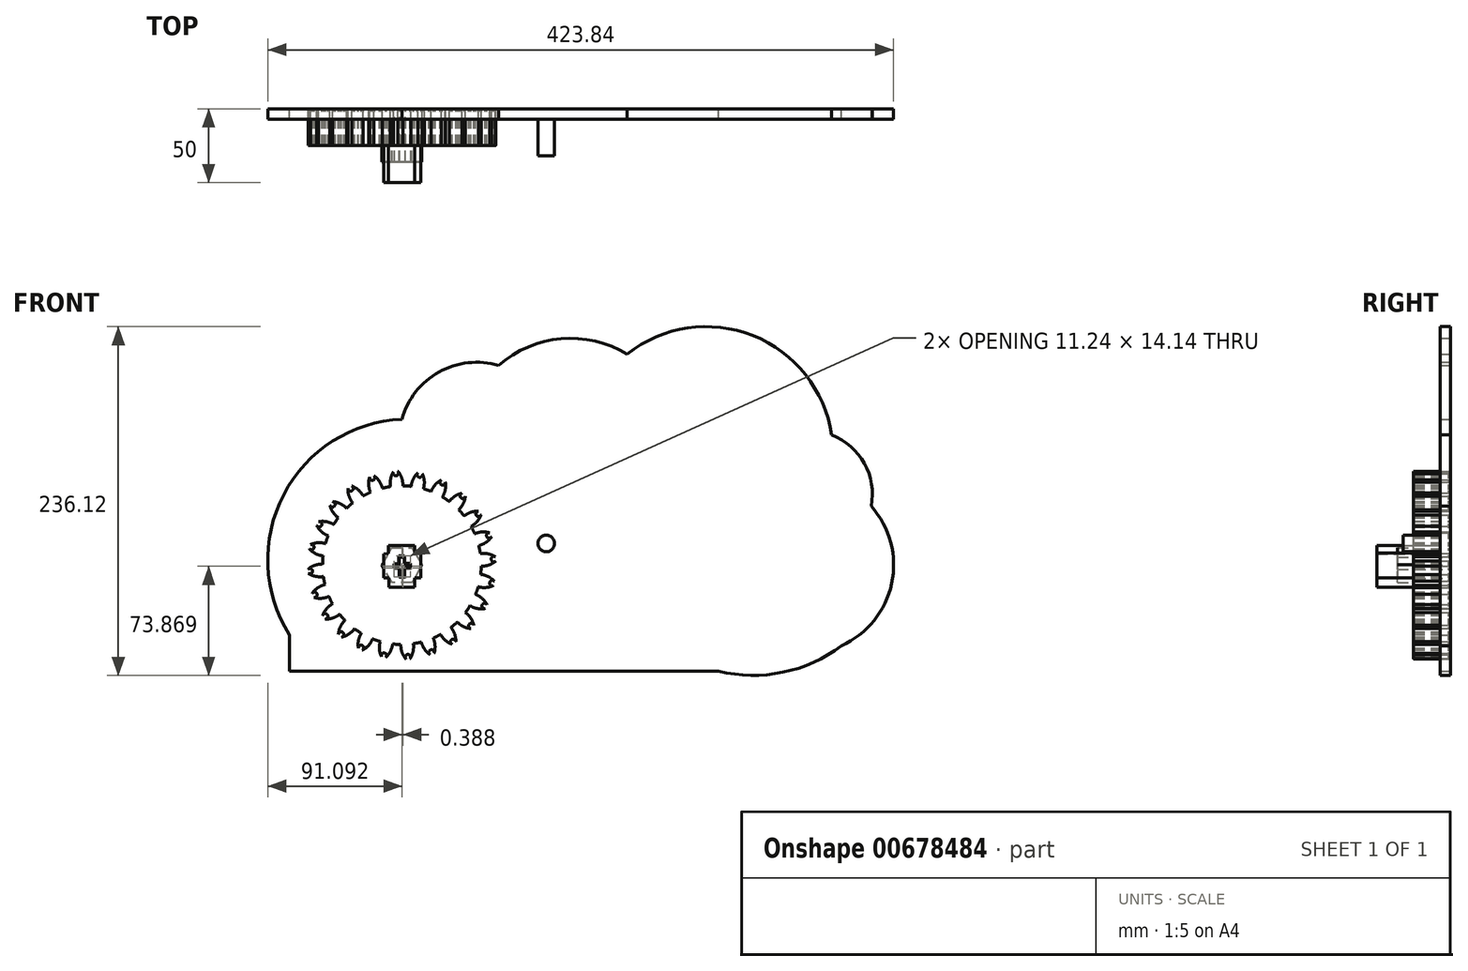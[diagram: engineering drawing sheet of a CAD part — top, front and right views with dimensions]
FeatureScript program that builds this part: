
annotation { "Feature Type Name" : "Feature", "Feature Type Description" : "" }
export const myFeature = defineFeature(function(context is Context, id is Id, definition is map)
    precondition{}
    {
        {
            var Q0;
            Q0=qCreatedBy(makeId("Front.planeOp"),FACE);
            var sketch = newSketch(context, id + "F0", { "sketchPlane" : qUnion([Q0])});
            skCircle(sketch, "E0", {"center": v(0, 0) * mm, "radius": 58.67 * mm, "construction": true});
            skCircle(sketch, "E1", {"center": v(0, 0) * mm, "radius": 53.72 * mm});
            skCircle(sketch, "E2", {"center": v(0, 0) * mm, "radius": 63.5 * mm, "construction": true});
            skLineSegment(sketch, "E3", {"start": v(0, 0) * mm, "end": v(0, 86.23) * mm, "construction": true});
            skLineSegment(sketch, "E4", {"start": v(0, 0) * mm, "end": v(-6, 91.64) * mm, "construction": true});
            skLineSegment(sketch, "E5", {"start": v(0, 58.67) * mm, "end": v(-65.6, 60.5) * mm, "construction": true});
            skLineSegment(sketch, "E6", {"start": v(0, 58.67) * mm, "end": v(-64.31, 37.28) * mm, "construction": true});
            skCircle(sketch, "E7", {"center": v(0, 0) * mm, "radius": 55.67 * mm, "construction": true});
            skCircle(sketch, "E8", {"center": v(0, 58.67) * mm, "radius": 14.6 * mm, "construction": true});
            skCircle(sketch, "E9", {"center": v(-13.86, 54.06) * mm, "radius": 14.6 * mm, "construction": true});
            skArc(sketch, "E10", {"start": v(0, 58.67) * mm, "mid": v(-1.1, 61.19) * mm, "end": v(-2.66, 63.44) * mm});
            skArc(sketch, "E11", {"start": v(0.74, 53.72) * mm, "mid": v(0.58, 56.23) * mm, "end": v(0, 58.67) * mm});
            skArc(sketch, "E12.MirrorCS", {"start": v(-7.66, 58.17) * mm, "mid": v(-6.9, 60.8) * mm, "end": v(-5.64, 63.25) * mm});
            skArc(sketch, "E13.MirrorCS", {"start": v(-7.75, 53.16) * mm, "mid": v(-7.91, 55.67) * mm, "end": v(-7.66, 58.17) * mm});
            skArc(sketch, "E14", {"start": v(-5.64, 63.25) * mm, "mid": v(-3.96, 60.49) * mm, "end": v(-2.66, 63.44) * mm});
            skCircle(sketch, "E15", {"center": v(0, 0) * mm, "radius": 37.66 * mm});
            skCircle(sketch, "E16.cCircle", {"center": v(0, 0) * mm, "radius": 13.56 * mm, "construction": true});
            skLineSegment(sketch, "E16.0", {"start": v(6.65, 11.81) * mm, "end": v(13.56, 0.15) * mm});
            skLineSegment(sketch, "E16.1", {"start": v(13.56, 0.15) * mm, "end": v(6.9, -11.66) * mm});
            skLineSegment(sketch, "E16.2", {"start": v(6.9, -11.66) * mm, "end": v(-6.65, -11.81) * mm});
            skLineSegment(sketch, "E16.3", {"start": v(-6.65, -11.81) * mm, "end": v(-13.56, -0.15) * mm});
            skLineSegment(sketch, "E16.4", {"start": v(-13.56, -0.15) * mm, "end": v(-6.9, 11.66) * mm});
            skLineSegment(sketch, "E16.5", {"start": v(-6.9, 11.66) * mm, "end": v(6.65, 11.81) * mm});
            skLineSegment(sketch, "E17", {"start": v(-1.68, 5.23) * mm, "end": v(2.17, 5.23) * mm});
            skLineSegment(sketch, "E18", {"start": v(2.17, 5.23) * mm, "end": v(2.17, 0) * mm});
            skLineSegment(sketch, "E19", {"start": v(-1.68, 5.23) * mm, "end": v(-1.68, 0) * mm});
            skLineSegment(sketch, "E20", {"start": v(2.17, 0) * mm, "end": v(6.24, 0) * mm});
            skLineSegment(sketch, "E21", {"start": v(6.24, 0) * mm, "end": v(6.24, -2.8) * mm});
            skLineSegment(sketch, "E22", {"start": v(6.24, -2.8) * mm, "end": v(2.17, -2.8) * mm});
            skLineSegment(sketch, "E23", {"start": v(2.17, -2.8) * mm, "end": v(2.17, -8.9) * mm});
            skLineSegment(sketch, "E24", {"start": v(2.17, -8.9) * mm, "end": v(-1.47, -8.9) * mm});
            skLineSegment(sketch, "E25", {"start": v(-1.47, -8.9) * mm, "end": v(-1.47, -2.8) * mm});
            skLineSegment(sketch, "E26", {"start": v(-1.47, -2.8) * mm, "end": v(-5, -2.8) * mm});
            skLineSegment(sketch, "E27", {"start": v(-5, -2.8) * mm, "end": v(-5, 0) * mm});
            skLineSegment(sketch, "E28", {"start": v(-5, -0.13) * mm, "end": v(-1.68, 0) * mm});
            skSolve(sketch);
        }
        {
            var Q0;
            {var subQ0=sQuery(id+"F0.wireOp",EDGE,"E1");var subQ1=makeQuery(id+"F0.imprint","INTERSECT",VERTEX,{"derivedFrom":[subQ0,sQuery(id+"F0.wireOp",EDGE,"E11")]});Q0=makeQuery(id+"F0.imprint","IMPRINT",FACE,{"disambiguationData":[TD([[makeQuery(id+"F0.imprint","IMPRINT",EDGE,{"disambiguationData":[TD([[subQ1,-1.0]])],"derivedFrom":subQ0}),1.0]])]});}
            var Q1;
            Q1=makeQuery(id+"F0.imprint","IMPRINT",FACE,{"disambiguationData":[TD([[makeQuery(id+"F0.imprint","IMPRINT",EDGE,{"derivedFrom":sQuery(id+"F0.wireOp",EDGE,"E10")}),1.0]])]});
            var Q2;
            Q2=makeQuery(id+"F0.imprint","IMPRINT",FACE,{"disambiguationData":[TD([[makeQuery(id+"F0.imprint","IMPRINT",EDGE,{"derivedFrom":sQuery(id+"F0.wireOp",EDGE,"E15")}),1.0]])]});
            extrude(context, id + "F1", {"entities" : qUnion([Q0, Q1, Q2]), "depth" : 25 * mm, "offsetDistance" : 25 * mm});
        }
        {
            var Q0;
            Q0=makeQuery(id+"F1.opExtrude","SWEPT_BODY",BODY,{"disambiguationData":[OSD([sQuery(id+"F0.wireOp",EDGE,"E1"),sQuery(id+"F0.wireOp",EDGE,"E10"),sQuery(id+"F0.wireOp",EDGE,"E11"),sQuery(id+"F0.wireOp",EDGE,"E12.MirrorCS"),sQuery(id+"F0.wireOp",EDGE,"E13.MirrorCS"),sQuery(id+"F0.wireOp",EDGE,"E14")])]});
            var Q1;
            Q1=makeQuery(id+"F1.opExtrude","SWEPT_FACE",FACE,{"disambiguationData":[OSD([sQuery(id+"F0.wireOp",EDGE,"E1")])]});
            circularPattern(context, id + "F2", {"entities" : qUnion([Q0]), "axis" : qUnion([Q1]), "angle" : 360 * degree, "instanceCount" : 24, "equalSpace" : true});
        }
        {
            var Q0;
            Q0=makeQuery(id+"F0.imprint","IMPRINT",FACE,{"disambiguationData":[TD([[makeQuery(id+"F0.imprint","IMPRINT",EDGE,{"derivedFrom":sQuery(id+"F0.wireOp",EDGE,"E16.0")}),-1.0]])]});
            extrude(context, id + "F3", {"entities" : qUnion([Q0]), "operationType" : NewBodyOperationType.ADD, "depth" : 36 * mm, "offsetDistance" : 25 * mm});
        }
        {
            var Q0;
            Q0=qCreatedBy(makeId("Front.planeOp"),FACE);
            var sketch = newSketch(context, id + "F4", { "sketchPlane" : qUnion([Q0])});
            skLineSegment(sketch, "E29", {"start": v(-76.16, -71.82) * mm, "end": v(215.95, -71.82) * mm});
            skLineSegment(sketch, "E30", {"start": v(-76.16, -71.82) * mm, "end": v(-76.16, -47.21) * mm});
            skArc(sketch, "E31", {"start": v(0, 98.8) * mm, "mid": v(-80.06, 47.7) * mm, "end": v(-76.16, -47.21) * mm});
            skArc(sketch, "E32", {"start": v(65.52, 135.17) * mm, "mid": v(25.12, 130.75) * mm, "end": v(0, 98.8) * mm});
            skArc(sketch, "E33", {"start": v(152.61, 142.93) * mm, "mid": v(107.8, 153.27) * mm, "end": v(65.52, 135.17) * mm});
            skArc(sketch, "E34", {"start": v(290.98, 88.07) * mm, "mid": v(237.63, 155.43) * mm, "end": v(152.61, 142.93) * mm});
            skArc(sketch, "E35", {"start": v(317.8, 39.91) * mm, "mid": v(313.19, 68.89) * mm, "end": v(290.98, 88.07) * mm});
            skArc(sketch, "E36", {"start": v(297.68, -54.57) * mm, "mid": v(331.67, -12.42) * mm, "end": v(317.8, 39.91) * mm});
            skArc(sketch, "E37", {"start": v(214.46, -71.82) * mm, "mid": v(258.02, -72.58) * mm, "end": v(297.68, -54.57) * mm});
            skLineSegment(sketch, "E38", {"start": v(-2.07, 6.3) * mm, "end": v(1.78, 6.3) * mm});
            skLineSegment(sketch, "E39", {"start": v(1.78, 6.3) * mm, "end": v(1.78, 1.07) * mm});
            skLineSegment(sketch, "E40", {"start": v(-2.07, 6.3) * mm, "end": v(-2.07, 1.07) * mm});
            skLineSegment(sketch, "E41", {"start": v(1.78, 1.07) * mm, "end": v(5.85, 1.07) * mm});
            skLineSegment(sketch, "E42", {"start": v(5.85, 1.07) * mm, "end": v(5.85, -1.74) * mm});
            skLineSegment(sketch, "E43", {"start": v(5.85, -1.74) * mm, "end": v(1.78, -1.74) * mm});
            skLineSegment(sketch, "E44", {"start": v(1.78, -1.74) * mm, "end": v(1.78, -7.84) * mm});
            skLineSegment(sketch, "E45", {"start": v(1.78, -7.84) * mm, "end": v(-1.86, -7.84) * mm});
            skLineSegment(sketch, "E46", {"start": v(-1.86, -7.84) * mm, "end": v(-1.86, -1.74) * mm});
            skLineSegment(sketch, "E47", {"start": v(-1.86, -1.74) * mm, "end": v(-5.4, -1.74) * mm});
            skLineSegment(sketch, "E48", {"start": v(-5.4, -1.74) * mm, "end": v(-5.4, 1.07) * mm});
            skLineSegment(sketch, "E49", {"start": v(-5.4, 0.94) * mm, "end": v(-2.07, 1.07) * mm});
            skSolve(sketch);
        }
        {
            var Q0;
            {var subQ0=sQuery(id+"F4.wireOp",EDGE,"E30");Q0=makeQuery(id+"F4.imprint","IMPRINT",FACE,{"disambiguationData":[TD([[makeQuery(id+"F4.imprint","IMPRINT",EDGE,{"derivedFrom":subQ0}),-1.0]])]});}
            extrude(context, id + "F5", {"entities" : qUnion([Q0]), "depth" : 50 * mm, "offsetDistance" : 25 * mm});
        }
        {
            var Q0;
            Q0=makeQuery(id+"F5.opExtrude","CAP_FACE",FACE,{"disambiguationData":[OSD([sQuery(id+"F4.wireOp",EDGE,"E29"),sQuery(id+"F4.wireOp",EDGE,"E30"),sQuery(id+"F4.wireOp",EDGE,"E31"),sQuery(id+"F4.wireOp",EDGE,"E32"),sQuery(id+"F4.wireOp",EDGE,"E33"),sQuery(id+"F4.wireOp",EDGE,"E34"),sQuery(id+"F4.wireOp",EDGE,"E35"),sQuery(id+"F4.wireOp",EDGE,"E36"),sQuery(id+"F4.wireOp",EDGE,"E37")])],"isStart":false});
            shell(context, id + "F6", {"entities" : qUnion([Q0]), "thickness" : 7 * mm});
        }
        {
            var Q0;
            Q0=makeQuery(id+"F5.opExtrude","CAP_FACE",FACE,{"disambiguationData":[OSD([sQuery(id+"F4.wireOp",EDGE,"E29"),sQuery(id+"F4.wireOp",EDGE,"E30"),sQuery(id+"F4.wireOp",EDGE,"E31"),sQuery(id+"F4.wireOp",EDGE,"E32"),sQuery(id+"F4.wireOp",EDGE,"E33"),sQuery(id+"F4.wireOp",EDGE,"E34"),sQuery(id+"F4.wireOp",EDGE,"E35"),sQuery(id+"F4.wireOp",EDGE,"E36"),sQuery(id+"F4.wireOp",EDGE,"E37"),sQuery(id+"F4.wireOp",EDGE,"E38"),sQuery(id+"F4.wireOp",EDGE,"E39"),sQuery(id+"F4.wireOp",EDGE,"E40"),sQuery(id+"F4.wireOp",EDGE,"E41"),sQuery(id+"F4.wireOp",EDGE,"E42"),sQuery(id+"F4.wireOp",EDGE,"E43"),sQuery(id+"F4.wireOp",EDGE,"E44"),sQuery(id+"F4.wireOp",EDGE,"E45"),sQuery(id+"F4.wireOp",EDGE,"E46"),sQuery(id+"F4.wireOp",EDGE,"E47"),sQuery(id+"F4.wireOp",EDGE,"E48"),sQuery(id+"F4.wireOp",EDGE,"E49")])],"isStart":false});
            extrude(context, id + "F7", {"entities" : qUnion([Q0]), "operationType" : NewBodyOperationType.REMOVE, "oppositeDirection" : true, "depth" : 43 * mm, "offsetDistance" : 25 * mm});
        }
        {
            var Q0;
            {var subQ0=sQuery(id+"F4.wireOp",EDGE,"E49");var subQ1=sQuery(id+"F4.wireOp",EDGE,"E48");var subQ2=sQuery(id+"F4.wireOp",EDGE,"E47");var subQ3=sQuery(id+"F4.wireOp",EDGE,"E46");var subQ4=sQuery(id+"F4.wireOp",EDGE,"E45");var subQ5=sQuery(id+"F4.wireOp",EDGE,"E44");var subQ6=sQuery(id+"F4.wireOp",EDGE,"E43");var subQ7=sQuery(id+"F4.wireOp",EDGE,"E42");var subQ8=sQuery(id+"F4.wireOp",EDGE,"E41");var subQ9=sQuery(id+"F4.wireOp",EDGE,"E40");var subQ10=sQuery(id+"F4.wireOp",EDGE,"E39");var subQ11=sQuery(id+"F4.wireOp",EDGE,"E38");var subQ12=sQuery(id+"F4.wireOp",EDGE,"E37");var subQ13=sQuery(id+"F4.wireOp",EDGE,"E36");var subQ14=sQuery(id+"F4.wireOp",EDGE,"E35");var subQ15=sQuery(id+"F4.wireOp",EDGE,"E34");var subQ16=sQuery(id+"F4.wireOp",EDGE,"E33");var subQ17=sQuery(id+"F4.wireOp",EDGE,"E32");var subQ18=sQuery(id+"F4.wireOp",EDGE,"E31");var subQ19=sQuery(id+"F4.wireOp",EDGE,"E30");var subQ20=sQuery(id+"F4.wireOp",EDGE,"E29");Q0=makeQuery(id+"F7.boolean.opBoolean","MERGE",FACE,{"derivedFrom":[makeQuery(id+"F6.opShell","OFFSET_FACE",FACE,{"disambiguationData":[OSD([subQ20,subQ19,subQ18,subQ17,subQ16,subQ15,subQ14,subQ13,subQ12,subQ11,subQ10,subQ9,subQ8,subQ7,subQ6,subQ5,subQ4,subQ3,subQ2,subQ1,subQ0]),TDD([makeQuery(id+"F5.opExtrude","CAP_FACE",FACE,{"disambiguationData":[OSD([subQ20,subQ19,subQ18,subQ17,subQ16,subQ15,subQ14,subQ13,subQ12,subQ11,subQ10,subQ9,subQ8,subQ7,subQ6,subQ5,subQ4,subQ3,subQ2,subQ1,subQ0])],"isStart":true})])]}),makeQuery(id+"F7.opExtrude","CAP_FACE",FACE,{"disambiguationData":[OSD([subQ20,subQ19,subQ18,subQ17,subQ16,subQ15,subQ14,subQ13,subQ12,subQ11,subQ10,subQ9,subQ8,subQ7,subQ6,subQ5,subQ4,subQ3,subQ2,subQ1,subQ0])],"isStart":false})]});}
            var sketch = newSketch(context, id + "F8", { "sketchPlane" : qUnion([Q0])});
            skCircle(sketch, "E50", {"center": v(97.78, 14.63) * mm, "radius": 5.6 * mm});
            skPoint(sketch, "E50.first.point", {"position": v(94.75, 19.34) * mm});
            skPoint(sketch, "E50.second.point", {"position": v(94.8, 19.37) * mm});
            skPoint(sketch, "E50.third.point", {"position": v(94.77, 19.34) * mm});
            skSolve(sketch);
        }
        {
            var Q0;
            Q0 = qSketchRegion(id + "F8", true);
            extrude(context, id + "F9", {"entities" : qUnion([Q0]), "operationType" : NewBodyOperationType.ADD, "depth" : 25 * mm, "offsetDistance" : 25 * mm});
        }
    });
